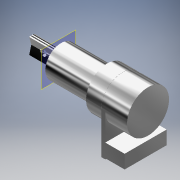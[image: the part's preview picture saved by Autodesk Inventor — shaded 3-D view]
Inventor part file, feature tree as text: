
AUTODESK INVENTOR PART (.ipt)
format: ipt  version: 2019.4 (Build 234330000, 330)  size: 239,616 bytes
history: native  units: mm
features: sketch x6, extrude x5, projected_geometry x4, revolve x1, plane x1, pattern_circular x1
ambient origin geometry x8: Origin, YZ Plane, XZ Plane, XY Plane, X Axis, Y Axis, Z Axis, Center Point
bodies: Solid1 (feature_tree)
feature tree (18):
  revolve  "Revolution1"  [1 undecoded]
  extrude  "Extrusion1"  Depth=0.05mm
  extrude  "Extrusion2"  TaperAngle=90.0deg  [1 undecoded]
  extrude  "Extrusion3"  TaperAngle=90.0deg  [1 undecoded]
  plane  "Work Plane1"
  extrude  "Extrusion4"  Depth=1.52mm
  extrude  "Extrusion5"  Depth=10.0mm
  pattern_circular  "Circular Pattern2"  Angle=90.0deg  [1 undecoded]
  sketch  "Sketch1"  dims[d0=8.675mm d1=9.0mm]
  sketch  "Sketch2"  dims[d2=0.0mm d3=0.05mm]
  projected_geometry  "Projected Loop1"
  sketch  "Sketch3"  dims[d4=1.62mm d5=90.0deg]
  projected_geometry  "Projected Loop2"
  sketch  "Sketch4"  dims[d6=6.32mm d7=90.0deg]
  projected_geometry  "Projected Loop3"
  sketch  "Sketch5"  dims[d8=3.62mm d9=1.52mm]
  sketch  "Sketch6"  dims[d10=1.42mm d11=17.5mm d12=90.0deg d13=90.0deg d14=17.325mm d15=17.35mm d16=10.0mm d17=0.0mm d18=8.0mm d19=0.0mm d20=1.5mm d21=8.0mm d22=0.0mm d23=1.0mm d24=0.5mm d25=6.8mm d26=11.0mm d27=0.0mm d31=11.0mm d32=0.0mm d33=30.0mm d34=30.0deg]
  projected_geometry  "Projected Loop4"
note: 4 required parameter values undecoded (feature->parameter linkage not recoverable at this tier; creation-order binding heuristic only, values carry confidence <= 0.55)